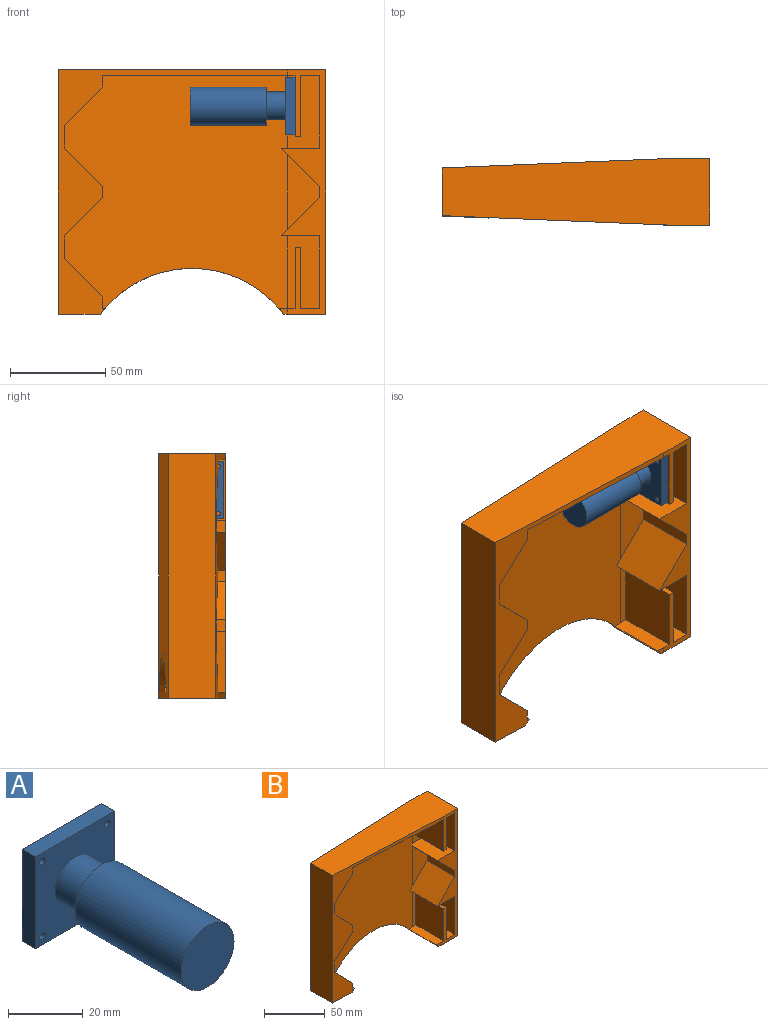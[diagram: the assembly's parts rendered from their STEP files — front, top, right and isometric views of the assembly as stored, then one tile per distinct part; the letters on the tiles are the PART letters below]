
ASSEMBLY  parts=2 mates=1
PART A: 14 faces, bbox 30x55x30 mm
  f0: plane 30x5mm, normal (0,0,-1), area 150mm2, adj f1,f3,f4,f5
  f1: plane 30x5mm, normal (1,0,0), area 150mm2, adj f0,f2,f4,f5
  f2: plane 30x5mm, normal (0,0,1), area 150mm2, adj f1,f3,f4,f5
  f3: plane 30x5mm, normal (-1,0,0), area 150mm2, adj f0,f2,f4,f5
  f4: plane 30x30mm, normal (0,-1,0), area 709.4mm2, adj f0,f1,f2,f3,f6,f10,f11,f12
  f5: plane 30x30mm, normal (0,1,0), area 886.1mm2, adj f0,f1,f2,f3,f10,f11,f12,f13
  f6: cylinder r=7.5mm len=15mm, axis (0,1,0), area 471.2mm2, adj f4,f9
  f7: cylinder r=10mm len=40mm, axis (0,1,0), area 2513.3mm2, adj f8,f9
  f8: plane 20x20mm, normal (0,-1,0), area 314.2mm2, adj f7
  f9: plane 20x20mm, normal (0,1,0), area 137.4mm2, adj f6,f7
  f10: cylinder r=1.05mm len=5mm, axis (0,-1,0), area 33mm2, adj f4,f5
  f11: cylinder r=1.05mm len=5mm, axis (0,-1,0), area 33mm2, adj f4,f5
  f12: cylinder r=1.05mm len=5mm, axis (0,-1,0), area 33mm2, adj f4,f5
  f13: cylinder r=1.05mm len=5mm, axis (0,-1,0), area 33mm2, adj f4,f5
PART B: 42 faces, bbox 140x35x128 mm
  f0: plane 32x8.4mm, normal (0,0,1), area 268.1mm2, adj f4,f15,f16,f17,f38,f41
  f1: plane 128x120mm, normal (-0.04,-1,0), area 1957.2mm2, adj f3,f5,f12,f13,f16,f18,f19,f20
  f2: plane 35x22mm, normal (0,0,-1), area 769.8mm2, adj f16,f17,f21,f22,f23,f41
  f3: plane 24.03x1.4mm, normal (0,0,1), area 33.7mm2, adj f1,f4,f40,f41
  f4: plane 122x117.06mm, normal (0.04,-1,0), area 11793.2mm2, adj f0,f3,f5,f10,f11,f12,f13,f15
  f5: plane 22.25x12mm, normal (1,0,0), area 267mm2, adj f1,f4,f30,f39
  f6: plane 32x10mm, normal (0,0,1), area 320mm2, adj f7,f15,f16,f36
  f7: plane 38x32mm, normal (-1,0,0), area 1216mm2, adj f6,f15,f16,f35
  f8: plane 32x6mm, normal (-1,0,0), area 192mm2, adj f10,f16,f33,f34
  f9: plane 38x32mm, normal (-1,0,0), area 1216mm2, adj f11,f14,f16,f32
  f10: plane 39.88x16.94mm, normal (0,-1,0), area 388.5mm2, adj f4,f8,f33,f34
  f11: plane 38x16.94mm, normal (0,-1,0), area 547.6mm2, adj f4,f9,f13,f14,f24,f25,f26,f32
  f12: plane 22.25x12mm, normal (1,0,0), area 267mm2, adj f1,f4,f28,f29
  f13: plane 101x32mm, normal (0,0,-1), area 2839.7mm2, adj f1,f4,f11,f16,f25,f27
  f14: plane 32x10mm, normal (0,0,-1), area 320mm2, adj f9,f11,f16,f24
  f15: plane 38x16.94mm, normal (0,-1,0), area 547.6mm2, adj f0,f4,f6,f7,f35,f36,f37,f38
  f16: plane 128x23mm, normal (0,-1,0), area 1078mm2, adj f0,f1,f2,f6,f7,f8,f9,f13
  f17: plane 4.41x3mm, normal (-0.04,-1,0), area 9.5mm2, adj f0,f2,f16,f41
  f18: plane 140x35mm, normal (0,0,1), area 4300mm2, adj f1,f16,f19,f21,f22,f23
  f19: plane 128x25mm, normal (-1,0,0), area 3200mm2, adj f1,f18,f20,f23
  f20: plane 26.83x22mm, normal (0,0,-1), area 570.2mm2, adj f1,f19,f23,f41
  f21: plane 128x35mm, normal (1,0,0), area 4480mm2, adj f2,f16,f18,f22
  f22: plane 128x20mm, normal (0,1,0), area 2560mm2, adj f2,f18,f21,f23
  f23: plane 128x120mm, normal (-0.04,1,0), area 13761.7mm2, adj f2,f18,f19,f20,f22,f41
  f24: plane 32x32mm, normal (1,0,0), area 1024mm2, adj f11,f14,f16,f26
  f25: plane 32x32mm, normal (-1,0,0), area 1024mm2, adj f11,f13,f16,f26
  f26: plane 32x3mm, normal (0,0,-1), area 96mm2, adj f11,f16,f24,f25
  f27: plane 23.91x6mm, normal (1,0,0), area 143.5mm2, adj f1,f4,f13,f28
  f28: plane 23.91x20mm, normal (0.71,0,-0.71), area 652.8mm2, adj f1,f4,f12,f27
  f29: plane 23.91x20mm, normal (0.71,0,0.71), area 652.8mm2, adj f1,f4,f12,f31
  f30: plane 23.91x20mm, normal (0.71,0,-0.71), area 652.8mm2, adj f1,f4,f5,f31
  f31: plane 23.91x6mm, normal (1,0,0), area 143.5mm2, adj f1,f4,f29,f30
  f32: plane 32x20mm, normal (0,0,1), area 639.8mm2, adj f4,f9,f11,f16,f33
  f33: plane 32x20mm, normal (-0.71,0,-0.71), area 904.8mm2, adj f4,f8,f10,f16,f32
  f34: plane 32x20mm, normal (-0.71,0,0.71), area 904.8mm2, adj f4,f8,f10,f16,f35
  f35: plane 32x20mm, normal (0,0,-1), area 639.8mm2, adj f4,f7,f15,f16,f34
  f36: plane 32x32mm, normal (1,0,0), area 1024mm2, adj f6,f15,f16,f37
  f37: plane 32x3mm, normal (0,0,1), area 96mm2, adj f15,f16,f36,f38
  f38: plane 32x32mm, normal (-1,0,0), area 1024mm2, adj f0,f15,f16,f37
  f39: plane 23.91x20mm, normal (0.71,0,0.71), area 652.8mm2, adj f1,f4,f5,f40
  f40: plane 23.91x6mm, normal (1,0,0), area 143.5mm2, adj f1,f3,f4,f39
  f41: cylinder r=60mm len=96mm, axis (0,-1,0), area 548.1mm2, adj f0,f1,f2,f3,f4,f17,f20,f23
PLACE A rot(axis=(-0.58,-0.58,-0.58),120deg) t=(44,-1.5,45)mm
PLACE B t=(-10,0,0)mm
MATE fastened A.f6 <-> B.f25  axis (1,0,0) through (44,-1.5,45)mm
